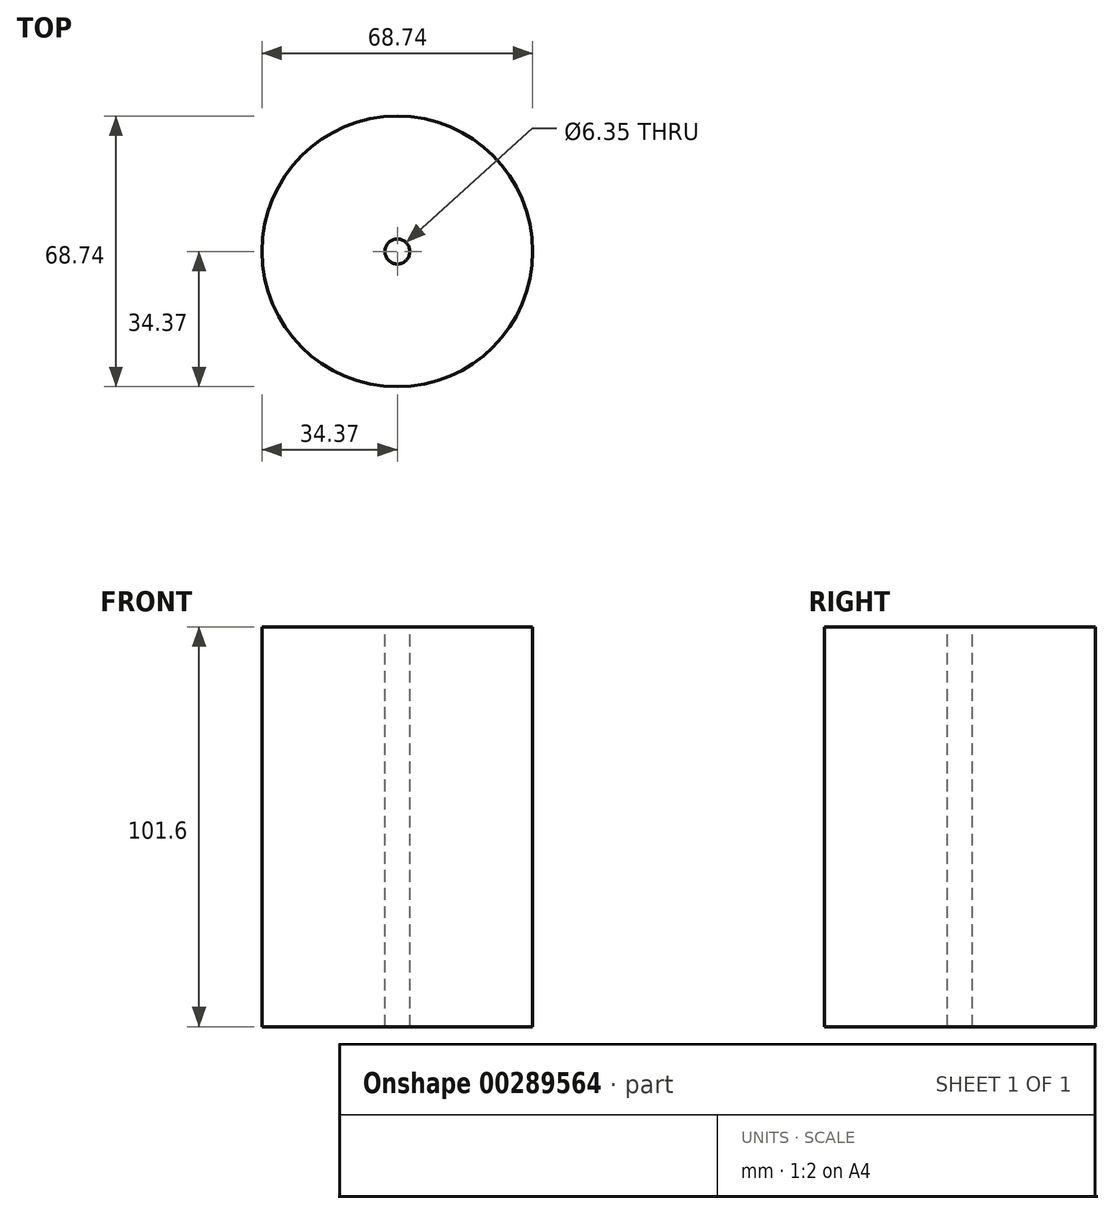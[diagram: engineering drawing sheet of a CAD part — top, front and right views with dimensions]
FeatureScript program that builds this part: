
annotation { "Feature Type Name" : "Feature", "Feature Type Description" : "" }
export const myFeature = defineFeature(function(context is Context, id is Id, definition is map)
    precondition{}
    {
        {
            var Q0;
            Q0=qCreatedBy(makeId("Top.planeOp"),FACE);
            var sketch = newSketch(context, id + "F0", { "sketchPlane" : qUnion([Q0])});
            skCircle(sketch, "E0", {"center": v(0, 0) * mm, "radius": 34.37 * mm});
            skSolve(sketch);
        }
        {
            var Q0;
            Q0=makeQuery(id+"F0.imprint","IMPRINT",FACE,{"disambiguationData":[TD([[makeQuery(id+"F0.imprint","IMPRINT",EDGE,{"derivedFrom":sQuery(id+"F0.wireOp",EDGE,"E0")}),1.0]])]});
            extrude(context, id + "F1", {"entities" : qUnion([Q0]), "depth" : 101.6 * mm});
        }
        {
            var Q0;
            Q0=makeQuery(id+"F1.opExtrude","CAP_FACE",FACE,{"disambiguationData":[OSD([sQuery(id+"F0.wireOp",EDGE,"E0")])],"isStart":false});
            var sketch = newSketch(context, id + "F2", { "sketchPlane" : qUnion([Q0])});
            skCircle(sketch, "E1", {"center": v(0, 0) * mm, "radius": 21.94 * mm});
            skSolve(sketch);
        }
        {
            var Q0;
            Q0=sQuery(id+"F2.wireOp",VERTEX,"E1.center");
            var Q1;
            Q1=makeQuery(id+"F1.opExtrude","SWEPT_BODY",BODY,{"disambiguationData":[OSD([sQuery(id+"F0.wireOp",EDGE,"E0")])]});
            hole(context, id + "F3", {"style" : HoleStyle.SIMPLE, "endStyle" : HoleEndStyle.THROUGH, "holeDiameter" : 6.35 * mm, "tappedDepth" : 12.7 * mm, "tapClearance" : 3, "locations" : qUnion([Q0]), "scope" : qUnion([Q1])});
        }
    });
